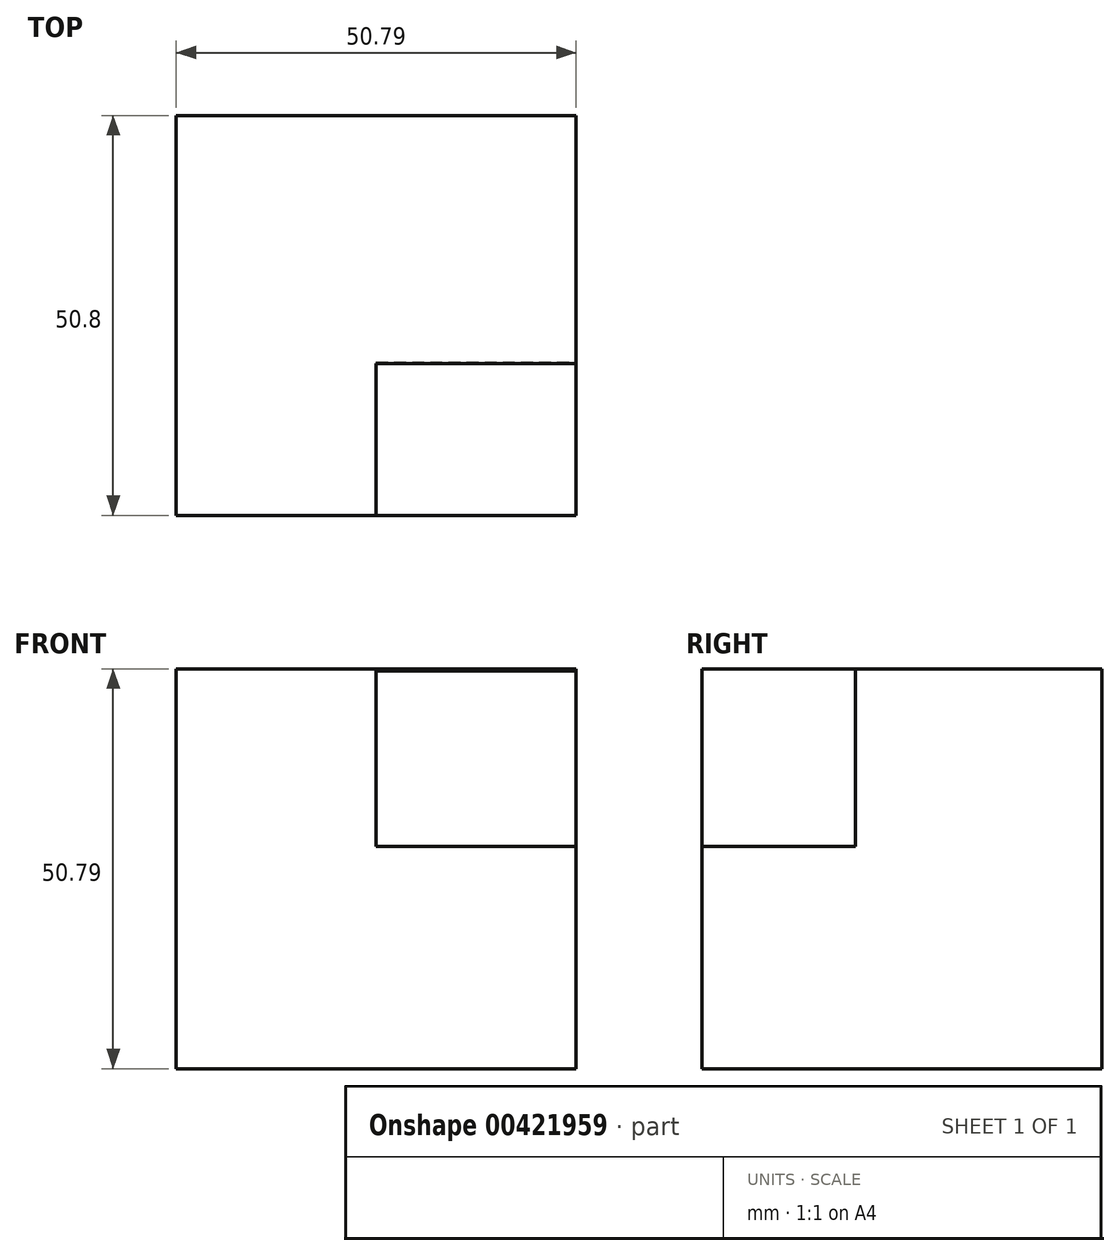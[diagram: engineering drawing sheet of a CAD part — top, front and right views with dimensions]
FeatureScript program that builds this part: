
annotation { "Feature Type Name" : "Feature", "Feature Type Description" : "" }
export const myFeature = defineFeature(function(context is Context, id is Id, definition is map)
    precondition{}
    {
        {
            var Q0;
            Q0=qCreatedBy(makeId("Front.planeOp"),FACE);
            var sketch = newSketch(context, id + "F0", { "sketchPlane" : qUnion([Q0])});
            skLineSegment(sketch, "E0", {"start": v(0, 0) * mm, "end": v(-50.8, 0) * mm});
            skLineSegment(sketch, "E1", {"start": v(-50.8, 0) * mm, "end": v(-50.8, 50.8) * mm});
            skLineSegment(sketch, "E2", {"start": v(-50.8, 50.8) * mm, "end": v(0, 50.8) * mm});
            skLineSegment(sketch, "E3", {"start": v(0, 50.8) * mm, "end": v(0, 0) * mm});
            skSolve(sketch);
        }
        {
            var Q0;
            Q0=makeQuery(id+"F0.imprint","IMPRINT",FACE,{"disambiguationData":[TD([[makeQuery(id+"F0.imprint","IMPRINT",EDGE,{"derivedFrom":sQuery(id+"F0.wireOp",EDGE,"E0")}),-1.0]])]});
            extrude(context, id + "F1", {"entities" : qUnion([Q0]), "depth" : 50.8 * mm});
        }
        {
            var Q0;
            Q0=qCreatedBy(makeId("Right.planeOp"),FACE);
            var sketch = newSketch(context, id + "F2", { "sketchPlane" : qUnion([Q0])});
            skLineSegment(sketch, "E4", {"start": v(-52.66, 79.12) * mm, "end": v(-72.91, 79.12) * mm});
            skLineSegment(sketch, "E5", {"start": v(-72.91, 79.12) * mm, "end": v(-72.91, 55.44) * mm});
            skLineSegment(sketch, "E6", {"start": v(-72.91, 55.44) * mm, "end": v(-51.04, 28.24) * mm});
            skLineSegment(sketch, "E7", {"start": v(-51.04, 28.24) * mm, "end": v(-31.33, 28.24) * mm});
            skLineSegment(sketch, "E8", {"start": v(-31.33, 28.24) * mm, "end": v(-31.33, 50.51) * mm});
            skLineSegment(sketch, "E9", {"start": v(-31.33, 50.51) * mm, "end": v(-52.66, 79.12) * mm});
            skSolve(sketch);
        }
        {
            var Q0;
            Q0=makeQuery(id+"F2.imprint","IMPRINT",FACE,{"disambiguationData":[TD([[makeQuery(id+"F2.imprint","IMPRINT",EDGE,{"derivedFrom":sQuery(id+"F2.wireOp",EDGE,"E4")}),1.0]])]});
            extrude(context, id + "F3", {"entities" : qUnion([Q0]), "operationType" : NewBodyOperationType.REMOVE, "oppositeDirection" : true, "depth" : 25.4 * mm});
        }
    });
